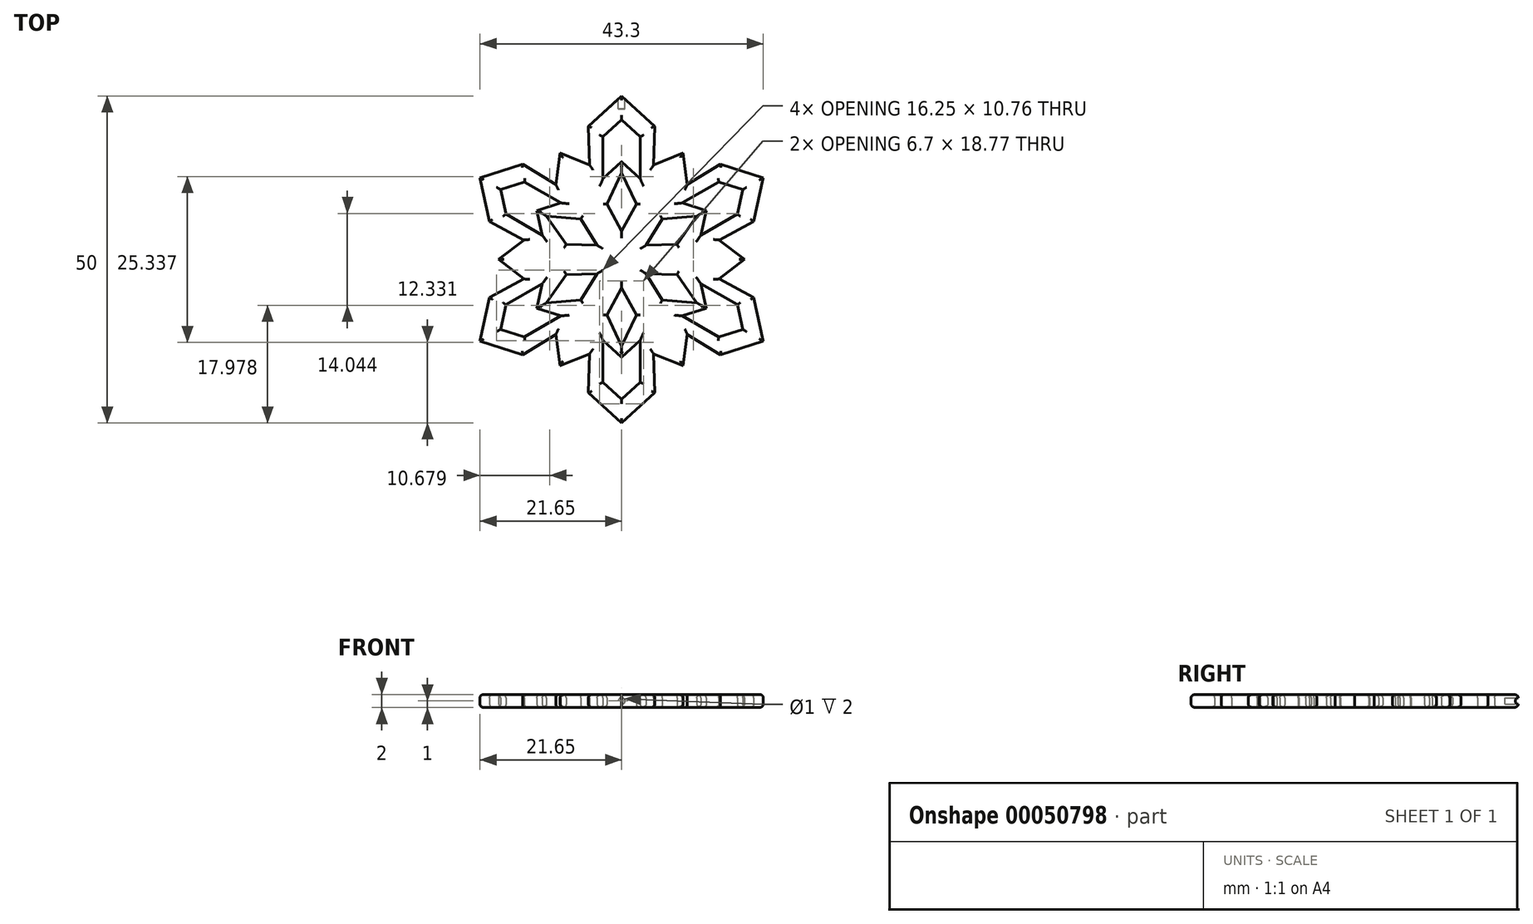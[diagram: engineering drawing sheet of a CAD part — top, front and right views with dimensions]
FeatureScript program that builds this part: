
annotation { "Feature Type Name" : "Feature", "Feature Type Description" : "" }
export const myFeature = defineFeature(function(context is Context, id is Id, definition is map)
    precondition{}
    {
        {
            var Q0;
            Q0=qCreatedBy(makeId("Top.planeOp"),FACE);
            var sketch = newSketch(context, id + "F0", { "sketchPlane" : qUnion([Q0])});
            skLineSegment(sketch, "E0", {"start": v(0, 0) * mm, "end": v(0, 29.9) * mm, "construction": true});
            skLineSegment(sketch, "E1", {"start": v(0, 0) * mm, "end": v(27.77, 16.03) * mm, "construction": true});
            skCircle(sketch, "E2", {"center": v(0, 0) * mm, "radius": 25 * mm, "construction": true});
            skLineSegment(sketch, "E3", {"start": v(0, 0) * mm, "end": v(18.78, 32.52) * mm, "construction": true});
            skLineSegment(sketch, "E4", {"start": v(0, 0) * mm, "end": v(-16.33, 28.28) * mm, "construction": true});
            skLineSegment(sketch, "E5", {"start": v(0, 25) * mm, "end": v(5.08, 20.38) * mm});
            skLineSegment(sketch, "E6", {"start": v(5.08, 20.38) * mm, "end": v(4.9, 14.43) * mm});
            skLineSegment(sketch, "E7", {"start": v(4.9, 14.43) * mm, "end": v(9.39, 16.26) * mm});
            skLineSegment(sketch, "E8", {"start": v(0, 13.26) * mm, "end": v(2.26, 8.5) * mm});
            skLineSegment(sketch, "E9.MirrorCS", {"start": v(-5.08, 20.38) * mm, "end": v(-4.9, 14.43) * mm});
            skLineSegment(sketch, "E10.MirrorCS", {"start": v(-4.9, 14.43) * mm, "end": v(-9.39, 16.26) * mm});
            skLineSegment(sketch, "E11.MirrorCS", {"start": v(0, 25) * mm, "end": v(-5.08, 20.38) * mm});
            skLineSegment(sketch, "E12.MirrorCS", {"start": v(0, 13.26) * mm, "end": v(-2.26, 8.5) * mm});
            skLineSegment(sketch, "E13", {"start": v(9.39, 16.26) * mm, "end": v(0, 0) * mm});
            skLineSegment(sketch, "E14", {"start": v(-9.39, 16.26) * mm, "end": v(0, 0) * mm});
            skLineSegment(sketch, "E15", {"start": v(2.26, 8.5) * mm, "end": v(0, 4.33) * mm});
            skLineSegment(sketch, "E16", {"start": v(0, 4.33) * mm, "end": v(-2.26, 8.5) * mm});
            skLineSegment(sketch, "E17", {"start": v(0, 21.38) * mm, "end": v(-2.85, 18.78) * mm});
            skLineSegment(sketch, "E18", {"start": v(-2.85, 18.78) * mm, "end": v(-2.85, 12.35) * mm});
            skLineSegment(sketch, "E19", {"start": v(-2.85, 12.35) * mm, "end": v(0, 14.95) * mm});
            skLineSegment(sketch, "E20.MirrorCS", {"start": v(2.85, 12.35) * mm, "end": v(0, 14.95) * mm});
            skLineSegment(sketch, "E21.MirrorCS", {"start": v(0, 21.38) * mm, "end": v(2.85, 18.78) * mm});
            skLineSegment(sketch, "E22.MirrorCS", {"start": v(2.85, 18.78) * mm, "end": v(2.85, 12.35) * mm});
            skSolve(sketch);
        }
        {
            var Q0;
            Q0=makeQuery(id+"F0.imprint","IMPRINT",FACE,{"disambiguationData":[TD([[makeQuery(id+"F0.imprint","IMPRINT",EDGE,{"derivedFrom":sQuery(id+"F0.wireOp",EDGE,"E5")}),-1.0]])]});
            extrude(context, id + "F1", {"entities" : qUnion([Q0]), "endBound" : BoundingType.SYMMETRIC, "depth" : 2 * mm});
        }
        {
            var Q0;
            Q0=qCreatedBy(makeId("Front.planeOp"),FACE);
            var sketch = newSketch(context, id + "F2", { "sketchPlane" : qUnion([Q0])});
            skLineSegment(sketch, "E23", {"start": v(0, -15.67) * mm, "end": v(0, 28.6) * mm, "construction": true});
            skSolve(sketch);
        }
        {
            var Q0;
            Q0=makeQuery(id+"F1.opExtrude","SWEPT_BODY",BODY,{"disambiguationData":[OSD([sQuery(id+"F0.wireOp",EDGE,"E5"),sQuery(id+"F0.wireOp",EDGE,"E6"),sQuery(id+"F0.wireOp",EDGE,"E7"),sQuery(id+"F0.wireOp",EDGE,"E8"),sQuery(id+"F0.wireOp",EDGE,"E9.MirrorCS"),sQuery(id+"F0.wireOp",EDGE,"E10.MirrorCS"),sQuery(id+"F0.wireOp",EDGE,"E11.MirrorCS"),sQuery(id+"F0.wireOp",EDGE,"E12.MirrorCS"),sQuery(id+"F0.wireOp",EDGE,"E13"),sQuery(id+"F0.wireOp",EDGE,"E14"),sQuery(id+"F0.wireOp",EDGE,"E15"),sQuery(id+"F0.wireOp",EDGE,"E16")])]});
            var Q1;
            Q1=sQuery(id+"F2.wireOp",EDGE,"E23");
            circularPattern(context, id + "F3", {"operationType" : NewBodyOperationType.ADD, "entities" : qUnion([Q0]), "axis" : qUnion([Q1]), "angle" : 360 * degree, "instanceCount" : round(6), "equalSpace" : true});
        }
        {
            var Q0;
            {var subQ0=makeQuery(id+"F1.opExtrude","CAP_FACE",FACE,{"disambiguationData":[OSD([sQuery(id+"F0.wireOp",EDGE,"E5"),sQuery(id+"F0.wireOp",EDGE,"E6"),sQuery(id+"F0.wireOp",EDGE,"E7"),sQuery(id+"F0.wireOp",EDGE,"E8"),sQuery(id+"F0.wireOp",EDGE,"E9.MirrorCS"),sQuery(id+"F0.wireOp",EDGE,"E10.MirrorCS"),sQuery(id+"F0.wireOp",EDGE,"E11.MirrorCS"),sQuery(id+"F0.wireOp",EDGE,"E12.MirrorCS"),sQuery(id+"F0.wireOp",EDGE,"E13"),sQuery(id+"F0.wireOp",EDGE,"E14"),sQuery(id+"F0.wireOp",EDGE,"E15"),sQuery(id+"F0.wireOp",EDGE,"E16")])],"isStart":false});Q0=makeQuery(id+"F3.boolean.opBoolean","MERGE",FACE,{"derivedFrom":[subQ0,makeQuery(id+"F3.opPattern","COPY",FACE,{"derivedFrom":subQ0,"instanceName":"1"}),makeQuery(id+"F3.opPattern","COPY",FACE,{"derivedFrom":subQ0,"instanceName":"2"}),makeQuery(id+"F3.opPattern","COPY",FACE,{"derivedFrom":subQ0,"instanceName":"3"}),makeQuery(id+"F3.opPattern","COPY",FACE,{"derivedFrom":subQ0,"instanceName":"4"}),makeQuery(id+"F3.opPattern","COPY",FACE,{"derivedFrom":subQ0,"instanceName":"5"})]});}
            var Q1;
            {var subQ0=makeQuery(id+"F1.opExtrude","CAP_FACE",FACE,{"disambiguationData":[OSD([sQuery(id+"F0.wireOp",EDGE,"E5"),sQuery(id+"F0.wireOp",EDGE,"E6"),sQuery(id+"F0.wireOp",EDGE,"E7"),sQuery(id+"F0.wireOp",EDGE,"E8"),sQuery(id+"F0.wireOp",EDGE,"E9.MirrorCS"),sQuery(id+"F0.wireOp",EDGE,"E10.MirrorCS"),sQuery(id+"F0.wireOp",EDGE,"E11.MirrorCS"),sQuery(id+"F0.wireOp",EDGE,"E12.MirrorCS"),sQuery(id+"F0.wireOp",EDGE,"E13"),sQuery(id+"F0.wireOp",EDGE,"E14"),sQuery(id+"F0.wireOp",EDGE,"E15"),sQuery(id+"F0.wireOp",EDGE,"E16")])],"isStart":true});Q1=makeQuery(id+"F3.boolean.opBoolean","MERGE",FACE,{"derivedFrom":[subQ0,makeQuery(id+"F3.opPattern","COPY",FACE,{"derivedFrom":subQ0,"instanceName":"1"}),makeQuery(id+"F3.opPattern","COPY",FACE,{"derivedFrom":subQ0,"instanceName":"2"}),makeQuery(id+"F3.opPattern","COPY",FACE,{"derivedFrom":subQ0,"instanceName":"3"}),makeQuery(id+"F3.opPattern","COPY",FACE,{"derivedFrom":subQ0,"instanceName":"4"}),makeQuery(id+"F3.opPattern","COPY",FACE,{"derivedFrom":subQ0,"instanceName":"5"})]});}
            fillet(context, id + "F4", {"entities" : qUnion([Q0, Q1]), "radius" : 0.5 * mm, "tangentPropagation" : true, "allowEdgeOverflow" : false});
        }
        {
            var Q0;
            Q0=qCreatedBy(makeId("Front.planeOp"),FACE);
            cPlane(context, id + "F5", {"entities" : qUnion([Q0]), "cplaneType" : CPlaneType.OFFSET, "offset" : 25 * mm, "oppositeDirection" : true, "width" : 150 * mm, "height" : 150 * mm});
        }
        {
            var Q0;
            Q0=qCreatedBy(id+"F5.planeOp",FACE);
            var sketch = newSketch(context, id + "F6", { "sketchPlane" : qUnion([Q0])});
            skCircle(sketch, "E24", {"center": v(0, 0) * mm, "radius": 0.5 * mm});
            skSolve(sketch);
        }
        {
            var Q0;
            Q0=makeQuery(id+"F6.imprint","IMPRINT",FACE,{"disambiguationData":[TD([[makeQuery(id+"F6.imprint","IMPRINT",EDGE,{"derivedFrom":sQuery(id+"F6.wireOp",EDGE,"E24")}),1.0]])]});
            extrude(context, id + "F7", {"entities" : qUnion([Q0]), "operationType" : NewBodyOperationType.REMOVE, "depth" : 2 * mm});
        }
    });
